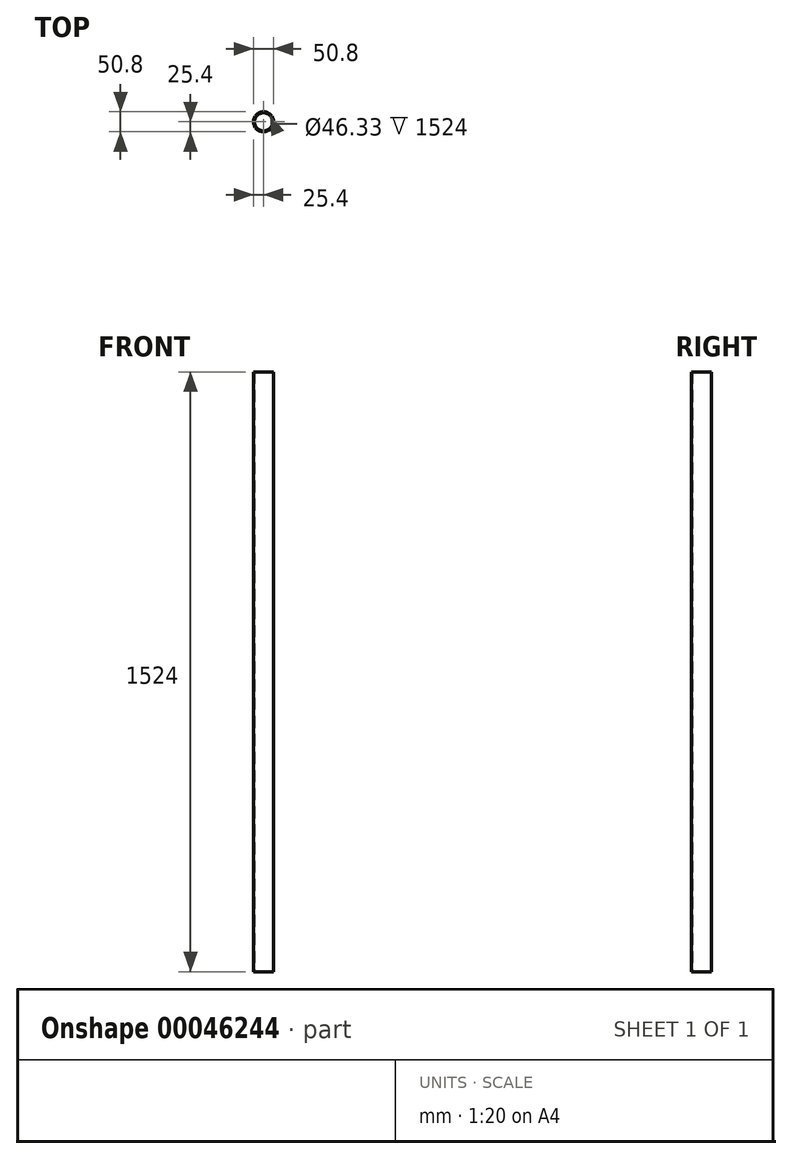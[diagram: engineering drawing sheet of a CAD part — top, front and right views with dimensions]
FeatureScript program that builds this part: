
annotation { "Feature Type Name" : "Feature", "Feature Type Description" : "" }
export const myFeature = defineFeature(function(context is Context, id is Id, definition is map)
    precondition{}
    {
        {
            var Q0;
            Q0=qCreatedBy(makeId("Top.planeOp"),FACE);
            var sketch = newSketch(context, id + "F0", { "sketchPlane" : qUnion([Q0])});
            skCircle(sketch, "E0", {"center": v(0, 0) * mm, "radius": 25.4 * mm});
            skCircle(sketch, "E1", {"center": v(0, 0) * mm, "radius": 23.16 * mm});
            skSolve(sketch);
        }
        {
            var Q0;
            Q0=makeQuery(id+"F0.imprint","IMPRINT",FACE,{"disambiguationData":[TD([[makeQuery(id+"F0.imprint","IMPRINT",EDGE,{"derivedFrom":sQuery(id+"F0.wireOp",EDGE,"E0")}),1.0]])]});
            extrude(context, id + "F1", {"entities" : qUnion([Q0]), "depth" : 1524 * mm});
        }
    });
